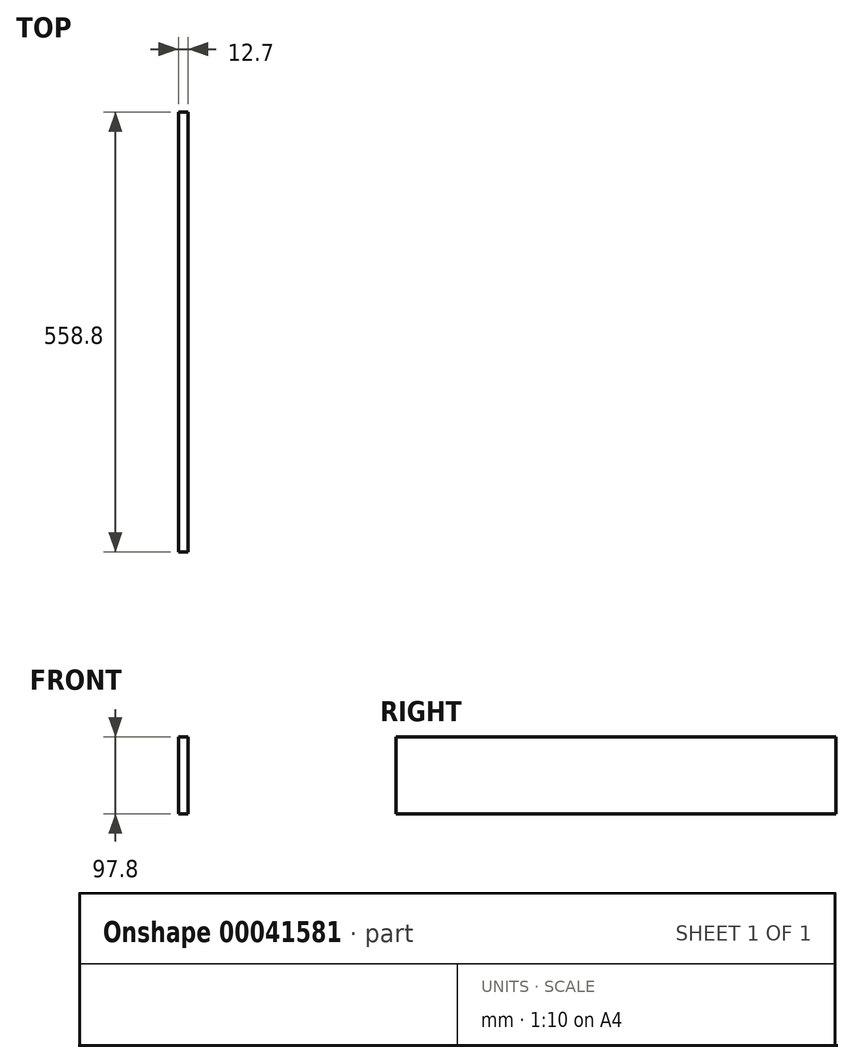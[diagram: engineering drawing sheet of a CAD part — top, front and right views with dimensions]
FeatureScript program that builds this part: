
annotation { "Feature Type Name" : "Feature", "Feature Type Description" : "" }
export const myFeature = defineFeature(function(context is Context, id is Id, definition is map)
    precondition{}
    {
        {
            var Q0;
            Q0=qCreatedBy(makeId("Front.planeOp"),FACE);
            var sketch = newSketch(context, id + "F0", { "sketchPlane" : qUnion([Q0])});
            skLineSegment(sketch, "E0.rect.bottom", {"start": v(6.35, 48.9) * mm, "end": v(-6.35, 48.9) * mm});
            skLineSegment(sketch, "E0.rect.top", {"start": v(6.35, -48.9) * mm, "end": v(-6.35, -48.9) * mm});
            skLineSegment(sketch, "E0.rect.left", {"start": v(6.35, 48.9) * mm, "end": v(6.35, -48.9) * mm});
            skLineSegment(sketch, "E0.rect.right", {"start": v(-6.35, 48.9) * mm, "end": v(-6.35, -48.9) * mm});
            skPoint(sketch, "E0.rect.middle", {"position": v(0, 0) * mm});
            skSolve(sketch);
        }
        {
            var Q0;
            Q0=makeQuery(id+"F0.imprint","IMPRINT",FACE,{"disambiguationData":[TD([[makeQuery(id+"F0.imprint","IMPRINT",EDGE,{"derivedFrom":sQuery(id+"F0.wireOp",EDGE,"E0.rect.bottom")}),1.0]])]});
            extrude(context, id + "F1", {"entities" : qUnion([Q0]), "depth" : 558.8 * mm});
        }
    });
